# Revit family: Bidet-WallMounted-Vitra_SentoSeries_5986B003-0288
name_source: partatom
category: Plumbing Fixtures
revit_build: Autodesk Revit 2017 (Build: 20160225_1515(x64)
units: mm (PartAtom-declared; Revit-internal decimal feet)

## family parameters
Cut with Voids When Loaded = No
Host = Face
OmniClass Number = 23.45.05.14.27
OmniClass Title = Bidets
Part Type = Normal
Room Calculation Point = No
Round Connector Dimension = Use Diameter
Shared = Yes

## types (1)
- Bidet_WallMountedBidet_Vitra_Sento_5986B003-0288
    Article No. (default) = 5986B003-0288
    BIMobject category = Bidets
    CW Connection = Yes
    Color = White
    Cost = 0 $
    Default Elevation = 410 mm  [stored 1.34514 ft]
    Description = Vitra Sento Wall Mounted Bidet
    Design country = Turkey
    HW Connection = Yes
    IFC Classification = Sanitary Terminal
    Installation instructions = https://cdn.vitra.com.tr
    Main Material = Ceramic
    Manufacturer = Vitra
    Manufacturer name = Vitra
    Masterformat 2014 Code = 22 41 13.19
    Masterformat 2014 Description = Residential Bidets
    Model = 5986B003-0288
    MountingType = Wall Mounted
    NBS Referans Code = 35-06-11
    NBS Referans Description = Bidets
    Nominal Depth (mm) = 540 mm  [stored 1.77165 ft]
    Nominal Height (mm) = 400 mm  [stored 1.31234 ft]
    Nominal Width (mm) = 365 mm  [stored 1.19751 ft]
    OmniClass Code = 23-31 23 00
    OmniClass Description = Bidets
    Product Guid = https://cdn.vitra.com.tr
    Product SKU = 5986B003-0288
    Product certification = https://vitraglobal.com
    Product data url = https://www.vitraglobal.com
    Product family = Sento
    Product group = Wall Mounted Bidet
    Secondary Material = Vitra-Ceramic-White
    Technical description = https://www.vitraglobal.com
    UNSPSC Code = 30181502
    UNSPSC Description = Sanitary Ware
    URL = https://www.vitra.com.tr
    Uniclass 1.4 Code = L7215
    Uniclass 1.4 Description = Bidets
    Uniclass 2.0 Code = PR-35-06-11
    Uniclass 2.0 Description = Bidets
    Uniclass 2015 Code = Pr_40_20_06_11
    Uniclass 2015 Name = Bidets
    Uniformat II Code = C10
    Uniformat II Description = Interior Construction
    Vent Connection = No
    Warranty Period (Year) = 10 Years
    Waste Connection = Yes
    Weight Net (kg) = 29,078
    Youtube = https://www.youtube.com

note: [stored X ft] marks values corroborated as IEEE doubles in the binary element streams (Revit-internal decimal feet)

## geometry (parser evidence)
native form markers: Sweep x2
no freeform markers — native parametric forms only
